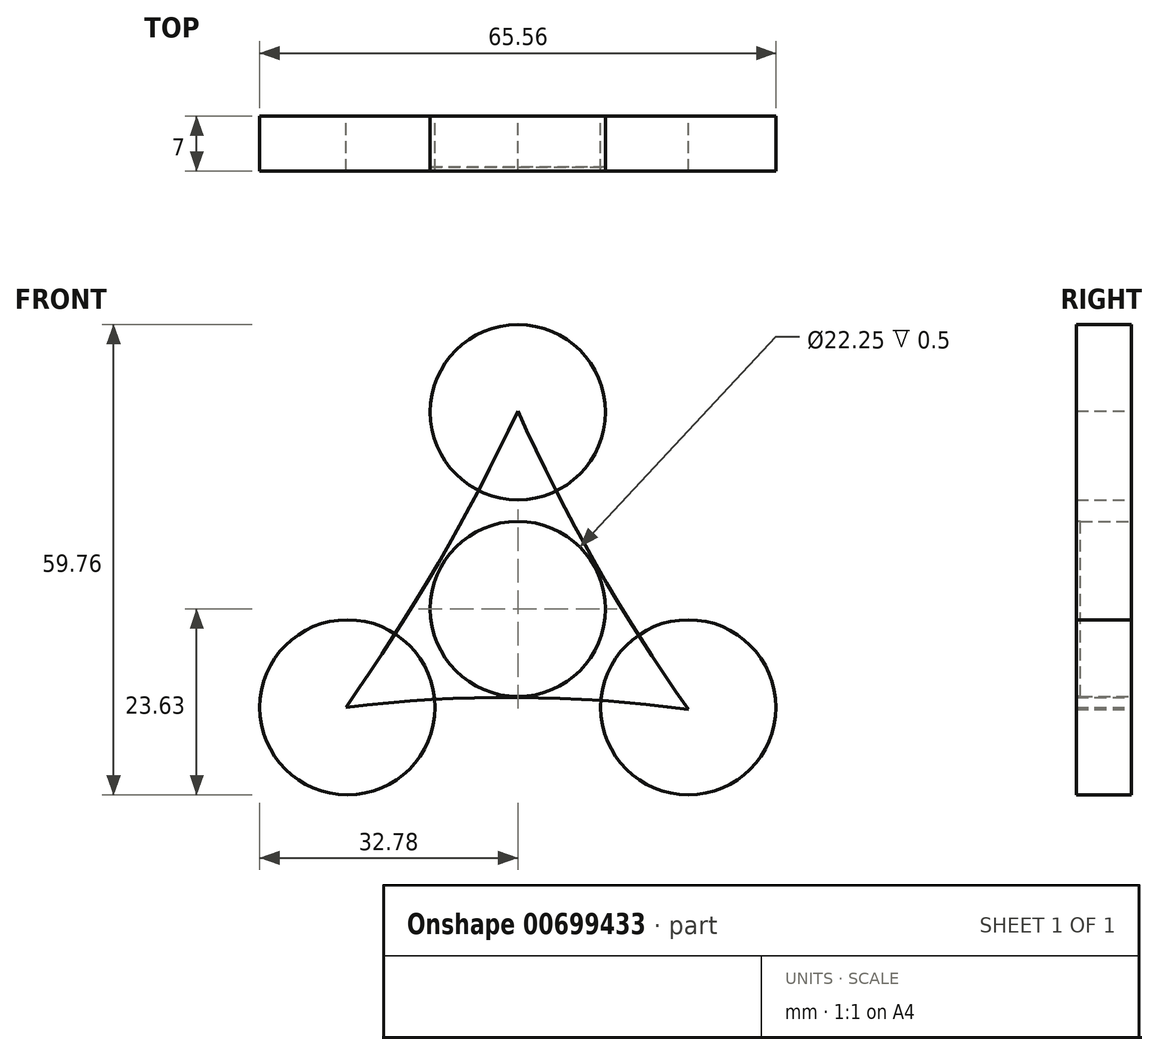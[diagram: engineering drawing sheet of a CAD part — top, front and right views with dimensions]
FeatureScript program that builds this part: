
annotation { "Feature Type Name" : "Feature", "Feature Type Description" : "" }
export const myFeature = defineFeature(function(context is Context, id is Id, definition is map)
    precondition{}
    {
        {
            var Q0;
            Q0=qCreatedBy(makeId("Front.planeOp"),FACE);
            var sketch = newSketch(context, id + "F0", { "sketchPlane" : qUnion([Q0])});
            skCircle(sketch, "E0", {"center": v(0, 0) * mm, "radius": 11.12 * mm});
            skCircle(sketch, "E1", {"center": v(0, 25) * mm, "radius": 11.12 * mm});
            skCircle(sketch, "E2", {"center": v(-21.65, -12.5) * mm, "radius": 11.12 * mm});
            skCircle(sketch, "E3", {"center": v(21.65, -12.5) * mm, "radius": 11.12 * mm});
            skLineSegment(sketch, "E4", {"start": v(0, 25) * mm, "end": v(0, 0) * mm});
            skLineSegment(sketch, "E5", {"start": v(0, 0) * mm, "end": v(21.65, -12.5) * mm});
            skLineSegment(sketch, "E6", {"start": v(0, 0) * mm, "end": v(-21.65, -12.5) * mm});
            skSolve(sketch);
        }
        {
            var Q0;
            Q0=qCreatedBy(makeId("Front.planeOp"),FACE);
            var sketch = newSketch(context, id + "F1", { "sketchPlane" : qUnion([Q0])});
            skArc(sketch, "E7", {"start": v(-21.84, -12.48) * mm, "mid": v(-10.09, 5.85) * mm, "end": v(0, 25.15) * mm});
            skArc(sketch, "E8", {"start": v(0, 25.15) * mm, "mid": v(9.9, 5.66) * mm, "end": v(21.68, -12.76) * mm});
            skArc(sketch, "E9", {"start": v(21.68, -12.76) * mm, "mid": v(-0.07, -11.24) * mm, "end": v(-21.84, -12.48) * mm});
            skSolve(sketch);
        }
        {
            var Q0;
            Q0 = qSketchRegion(id + "F0", true);
            extrude(context, id + "F2", {"entities" : qUnion([Q0]), "depth" : 7 * mm, "offsetDistance" : 25 * mm});
        }
        {
            var Q0;
            Q0 = qSketchRegion(id + "F1", true);
            extrude(context, id + "F3", {"entities" : qUnion([Q0]), "depth" : 7 * mm, "offsetDistance" : 25 * mm});
        }
        {
            var Q0;
            Q0=qCreatedBy(makeId("Front.planeOp"),FACE);
            var sketch = newSketch(context, id + "F4", { "sketchPlane" : qUnion([Q0])});
            skCircle(sketch, "E10", {"center": v(0, 0) * mm, "radius": 11 * mm});
            skSolve(sketch);
        }
        {
            var Q0;
            Q0 = qSketchRegion(id + "F4", true);
            extrude(context, id + "F5", {"entities" : qUnion([Q0]), "operationType" : NewBodyOperationType.REMOVE, "oppositeDirection" : true, "depth" : 7 * mm, "offsetDistance" : 25 * mm});
        }
        {
            var Q0;
            Q0=makeQuery(id+"F2.opExtrude","CAP_FACE",FACE,{"disambiguationData":[OSD([sQuery(id+"F0.wireOp",EDGE,"E0")])],"isStart":false});
            extrude(context, id + "F6", {"entities" : qUnion([Q0]), "operationType" : NewBodyOperationType.REMOVE, "oppositeDirection" : true, "depth" : .5 * mm, "offsetDistance" : 25 * mm});
        }
    });
